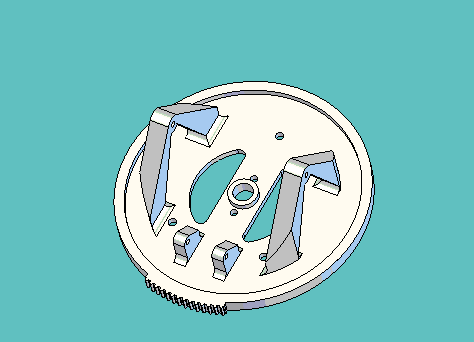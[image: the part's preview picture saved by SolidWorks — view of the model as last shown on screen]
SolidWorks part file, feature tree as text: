
SOLIDWORKS PART (.sldprt)
format: sldprt  version: not decoded by parser v0  size: 2,203,136 bytes
history: native  units: mm
features: sketch x16, cut_extrude x9, extrude x7, plane x7, fillet x2, material x1 (+11 scaffold rows collapsed)
feature tree (53):
  scaffold x11  (default folders/planes/origin — collapsed)
  material  "Material <not specified>"
  sketch  "Sketch1"  dims[c1.D1=50.8mm c1.D7=3.175mm c2.D1=89.1032mm c2.D2=~93.32036mm c3.D2=45.0deg c3.D3=~94.913632mm c4.D3=45.0deg c4.D4=6.35mm c4.D5=6.35mm c4.D6=31.75mm]
  extrude  "Extrude1"  Depth=6.35mm
  sketch  "Sketch2"  dims[c1.D1=50.8mm c1.D7=~3.96875mm c2.D1=~3.96875mm c2.D4=~3.96875mm c2.D6=69.85mm c2.D2=~93.32036mm c3.D2=163.0deg c3.D3=~94.913632mm c4.D3=45.0deg c4.D4=4.7625mm c4.D5=4.7625mm c4.D6=31.75mm c4.D1=4.7625mm c5.D6=34.925mm c5.D2=~82.034109mm c6.D2=30.0deg c6.D3=~82.034109mm c7.D3=107.0deg c7.D5=~82.034109mm c8.D5=167.0deg]
  cut_extrude  "Cut-Extrude8"  [1 undecoded]
  sketch  "Sketch3"  dims[c1.D1=3.4544mm c1.D2=3.4544mm c1.D3=9.525mm c1.D5=~19.84375mm c1.D4=~65.353861mm c2.D4=30.0deg]
  cut_extrude  "Cut-Extrude2"  [1 undecoded]
  sketch  "Sketch5"  dims[c1.D3=19.05mm c1.D4=25.4mm c1.D1=20.6375mm c1.D2=20.6375mm c1.D5=~49.79749mm c2.D5=30.0deg c2.D6=11.1125mm c2.D1=17.145mm c2.D2=17.145mm c3.D1=~82.457251mm c4.D1=90.0deg c4.D2=9.525mm c4.D3=9.525mm]
  cut_extrude  "Cut-Extrude4"  [1 undecoded]
  fillet  "Fillet2"  Radius=3.175mm
  sketch  "Sketch6"  dims[D1=9.525mm]
  extrude  "Axis2"  [1 undecoded]
  plane  "Plane1"
  plane  "Plane2"
  plane  "Plane3"  Offset=50.8mm
  sketch  "Sketch11"  dims[c1.D1=40.3225mm c1.D2=40.3225mm c2.D1=22.86mm c2.D2=24.384mm c2.D3=30.1625mm c2.D4=30.1625mm]
  extrude  "Extrude6"  Depth=44.45mm
  sketch  "Sketch7"  dims[D1=2.7051mm D2=4.7625mm]
  cut_extrude  "Cut-Extrude7"  [1 undecoded]
  sketch  "Sketch12"  dims[D1=6.35mm D2=6.35mm D3=6.35mm]
  cut_extrude  "Cut-Extrude9"  [1 undecoded]
  sketch  "Sketch15"  dims[c1.D4=3.175mm c1.D1=9.525mm c1.D2=9.525mm c1.D3=9.525mm c2.D1=9.525mm c2.D2=9.525mm c2.D5=25.4mm c2.D6=25.4mm c2.D3=~20.134035mm c2.D4=~20.134035mm]
  cut_extrude  "Cut-Extrude12"  [1 undecoded]
  plane  "Plane4"  Offset=7.14375mm
  plane  "Plane5"  Offset=7.14375mm
  sketch  "Sketch17"  dims[c1.D4=2.7051mm c1.D1=28.575mm c1.D2=9.525mm c1.D3=6.35mm c2.D1=38.1mm c2.D5=~9.745748mm c2.D3=9.525mm c3.D5=6.35mm c3.D6=3.175mm c3.D2=~11.90625mm c4.D5=~8.73125mm c4.D7=4.7625mm]
  extrude  "Extrude8"  Depth=5.969mm
  sketch  "Sketch18"  dims[D1=0.0mm]
  extrude  "Extrude9"  Depth=5.969mm
  plane  "Plane6"  Offset=39.6875mm
  plane  "Plane7"  Offset=39.6875mm
  sketch  "Sketch19"  dims[D1=12.7mm]
  cut_extrude  "Cut-Extrude14"  [1 undecoded]
  sketch  "Sketch20"
  cut_extrude  "Cut-Extrude15"  [1 undecoded]
  sketch  "Sketch22"  dims[D1=119.38mm]
  extrude  "Extrude10"  [1 undecoded]
  sketch  "Sketch23"  dims[c1.D1=~112.042099mm c1.D2=9.525mm c2.D1=4.7625mm c2.D2=~2.38125mm]
  cut_extrude  "Cut-Extrude16"  Depth=3.175mm
  fillet  "Fillet3"  Radius=3.175mm
  sketch  "Sketch24"  dims[c1.D1=~90.71926mm c1.D4=~45.35963mm c2.D1=~45.35963mm c2.D4=~45.35963mm c2.D5=~45.35963mm c2.D9=2.0422mm c3.D1=61.1124mm c3.D12=119.38mm c3.D2=~55.294757mm c4.D2=30.0deg c4.D3=~55.294757mm c5.D3=30.0deg c5.D4=~45.35963mm c5.D1=~2.999484mm c6.D4=~45.35963mm c6.D5=~45.35963mm c6.D2=0.809mm c6.D3=2.41mm c6.D6=1.19mm c6.D7=0.324mm c6.D8=0.1944mm c6.D9=0.1944mm c6.D10=1.19mm c7.D2=0.381mm c7.D3=1.2192mm c7.D4=3.0226mm c7.D5=0.3302mm c7.D6=~49.397463mm c8.D6=~1.40625deg c8.D7=~49.397463mm c9.D7=~1.40625deg c9.D8=~0.11938mm c9.D9=~0.11938mm c9.D10=~0.19558mm c9.D11=~0.19558mm c9.D13=~49.397463mm c10.D13=60.0deg c10.D14=~81.691281mm c11.D14=~19.21875deg c11.D15=~81.691281mm c12.D15=~20.15625deg c12.D2=~81.691281mm c13.D2=60.0deg c13.D4=~282.002929mm c13.D1=~282.002929mm c14.D4=3.0mm c14.D5=1.5mm c14.D2=0.8128mm]
  extrude  "Extrude11"  [1 undecoded]
decode coverage: 22 of 34 modeling features carry decoded parameters
note: ~ marks probable driven/reference dimensions
note: 11 parameter values undecoded
summary: no parameter record found for 11 features
note: suppression state not decoded; provenance and decode notes live in map.json
